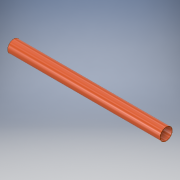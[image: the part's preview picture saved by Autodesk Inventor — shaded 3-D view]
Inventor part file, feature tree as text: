
AUTODESK INVENTOR PART (.ipt)
format: ipt  version: 2017 SP1 (Build 210196100, 196)  size: 98,816 bytes
history: native  units: in
note: dims shown in document units (in); Inventor stores cm internally (conversion verified against a paired STEP export)
features: extrude x1, sketch x1
ambient origin geometry x8: Origin, YZ Plane, XZ Plane, XY Plane, X Axis, Y Axis, Z Axis, Center Point
bodies: Solid1 (feature_tree)
feature tree (2):
  extrude  "Extrusion1"  Depth=91.5in
  sketch  "Sketch1"  dims[d0=7.4in d1=7.15in d2=91.5in d3=0.0in]
